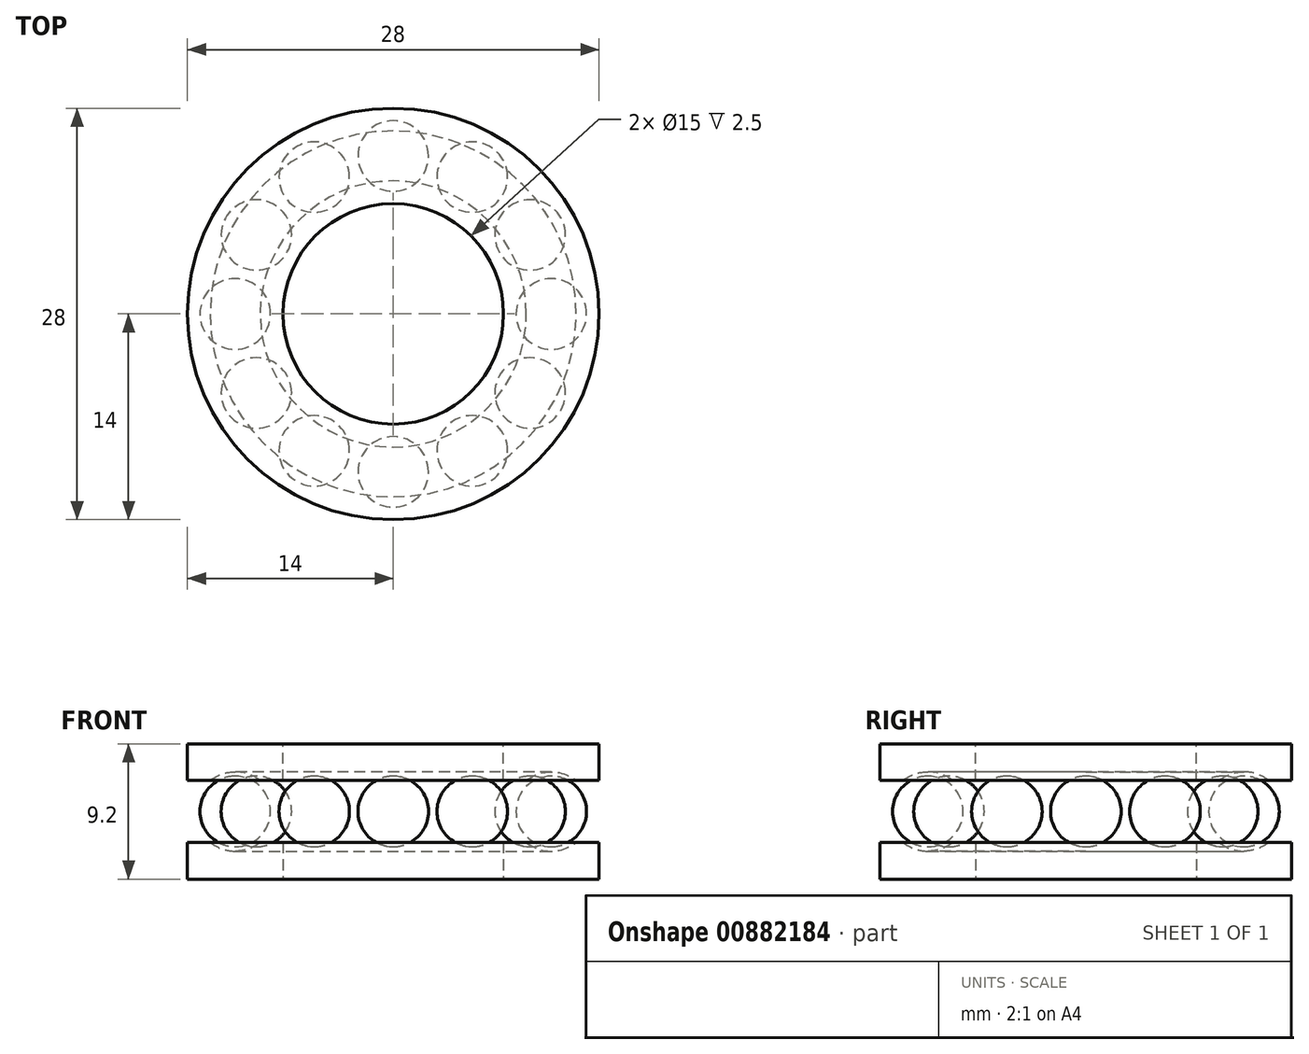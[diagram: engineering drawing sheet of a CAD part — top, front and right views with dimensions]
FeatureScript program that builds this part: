
annotation { "Feature Type Name" : "Feature", "Feature Type Description" : "" }
export const myFeature = defineFeature(function(context is Context, id is Id, definition is map)
    precondition{}
    {
        {
            var Q0;
            Q0=qCreatedBy(makeId("Top.planeOp"),FACE);
            var sketch = newSketch(context, id + "F0", { "sketchPlane" : qUnion([Q0])});
            skCircle(sketch, "E0", {"center": v(0, 0) * mm, "radius": 14 * mm});
            skCircle(sketch, "E1", {"center": v(0, 0) * mm, "radius": 7.5 * mm});
            skSolve(sketch);
        }
        {
            var Q0;
            Q0 = qSketchRegion(id + "F0", true);
            extrude(context, id + "F1", {"entities" : qUnion([Q0]), "depth" : 2.5 * mm, "offsetDistance" : 25 * mm});
        }
        {
            var Q0;
            Q0=qCreatedBy(makeId("Front.planeOp"),FACE);
            var sketch = newSketch(context, id + "F2", { "sketchPlane" : qUnion([Q0])});
            skLineSegment(sketch, "E2", {"start": v(-14, 2.5) * mm, "end": v(14, 2.5) * mm, "construction": true});
            skPoint(sketch, "E3", {"position": v(0, 2.5) * mm});
            skLineSegment(sketch, "E4.bottom", {"start": v(-14, 2.5) * mm, "end": v(-7.5, 2.5) * mm, "construction": true});
            skLineSegment(sketch, "E4.top", {"start": v(-14, 0) * mm, "end": v(-7.5, 0) * mm, "construction": true});
            skLineSegment(sketch, "E4.left", {"start": v(-14, 2.5) * mm, "end": v(-14, 0) * mm, "construction": true});
            skLineSegment(sketch, "E4.right", {"start": v(-7.5, 2.5) * mm, "end": v(-7.5, 0) * mm, "construction": true});
            skArc(sketch, "E5", {"start": v(-12.45, 2.5) * mm, "mid": v(-10.75, 1.9) * mm, "end": v(-9.05, 2.5) * mm});
            skPoint(sketch, "E6", {"position": v(-10.75, 2.5) * mm});
            skLineSegment(sketch, "E7", {"start": v(-12.45, 2.5) * mm, "end": v(-9.05, 2.5) * mm});
            skCircle(sketch, "E8", {"center": v(-10.75, 4.6) * mm, "radius": 2.7 * mm, "construction": true});
            skSolve(sketch);
        }
        {
            var Q0;
            Q0=makeQuery(id+"F2.imprint","IMPRINT",FACE,{"disambiguationData":[TD([[makeQuery(id+"F2.imprint","IMPRINT",EDGE,{"derivedFrom":sQuery(id+"F2.wireOp",EDGE,"E5")}),1.0]])]});
            var Q1;
            Q1=makeQuery(id+"F1.opExtrude","SWEPT_FACE",FACE,{"disambiguationData":[OSD([sQuery(id+"F0.wireOp",EDGE,"E1")])]});
            revolve(context, id + "F3", {"operationType" : NewBodyOperationType.REMOVE, "surfaceOperationType" : NewSurfaceOperationType.NEW, "entities" : qUnion([Q0]), "axis" : qUnion([Q1]), "revolveType" : RevolveType.FULL, "oppositeDirection" : true});
        }
        {
            var Q0;
            Q0=qCreatedBy(makeId("Front.planeOp"),FACE);
            var sketch = newSketch(context, id + "F4", { "sketchPlane" : qUnion([Q0])});
            skArc(sketch, "E9", {"start": v(-10.75, 7) * mm, "mid": v(-13.15, 4.6) * mm, "end": v(-10.75, 2.2) * mm});
            skLineSegment(sketch, "E10", {"start": v(-10.75, 4.6) * mm, "end": v(-10.75, 7) * mm});
            skLineSegment(sketch, "E11", {"start": v(-10.75, 4.6) * mm, "end": v(-10.75, 2.2) * mm});
            skSolve(sketch);
        }
        {
            var Q0;
            Q0=makeQuery(id+"F4.imprint","IMPRINT",FACE,{"disambiguationData":[TD([[makeQuery(id+"F4.imprint","IMPRINT",EDGE,{"derivedFrom":sQuery(id+"F4.wireOp",EDGE,"E9")}),1.0]])]});
            var Q1;
            Q1=sQuery(id+"F4.wireOp",EDGE,"E10");
            revolve(context, id + "F5", {"surfaceOperationType" : NewSurfaceOperationType.NEW, "entities" : qUnion([Q0]), "axis" : qUnion([Q1]), "revolveType" : RevolveType.FULL});
        }
        {
            var Q0;
            Q0=makeQuery(id+"F5.opRevolve","SWEPT_BODY",BODY,{"disambiguationData":[OSD([sQuery(id+"F4.wireOp",EDGE,"E9"),sQuery(id+"F4.wireOp",EDGE,"E10"),sQuery(id+"F4.wireOp",EDGE,"E11")])]});
            var Q1;
            Q1=makeQuery(id+"F1.opExtrude","CAP_EDGE",EDGE,{"disambiguationData":[OSD([sQuery(id+"F0.wireOp",EDGE,"E1")])],"isStart":false});
            circularPattern(context, id + "F6", {"entities" : qUnion([Q0]), "axis" : qUnion([Q1]), "angle" : 360 * degree, "instanceCount" : 12, "equalSpace" : true});
        }
        {
            var Q0;
            Q0=qCreatedBy(makeId("Top.planeOp"),FACE);
            var Q1;
            Q1=sQuery(id+"F2.wireOp",VERTEX,"E5.center");
            cPlane(context, id + "F7", {"entities" : qUnion([Q0, Q1]), "cplaneType" : CPlaneType.PLANE_POINT, "offset" : 25 * mm, "width" : 150 * mm, "height" : 150 * mm});
        }
        {
            var Q0;
            Q0=makeQuery(id+"F1.opExtrude","SWEPT_BODY",BODY,{"disambiguationData":[OSD([sQuery(id+"F0.wireOp",EDGE,"E0"),sQuery(id+"F0.wireOp",EDGE,"E1")])]});
            var Q1;
            Q1=qCreatedBy(id+"F7.planeOp",FACE);
            mirror(context, id + "F8", {"entities" : qUnion([Q0]), "mirrorPlane" : qUnion([Q1])});
        }
    });
